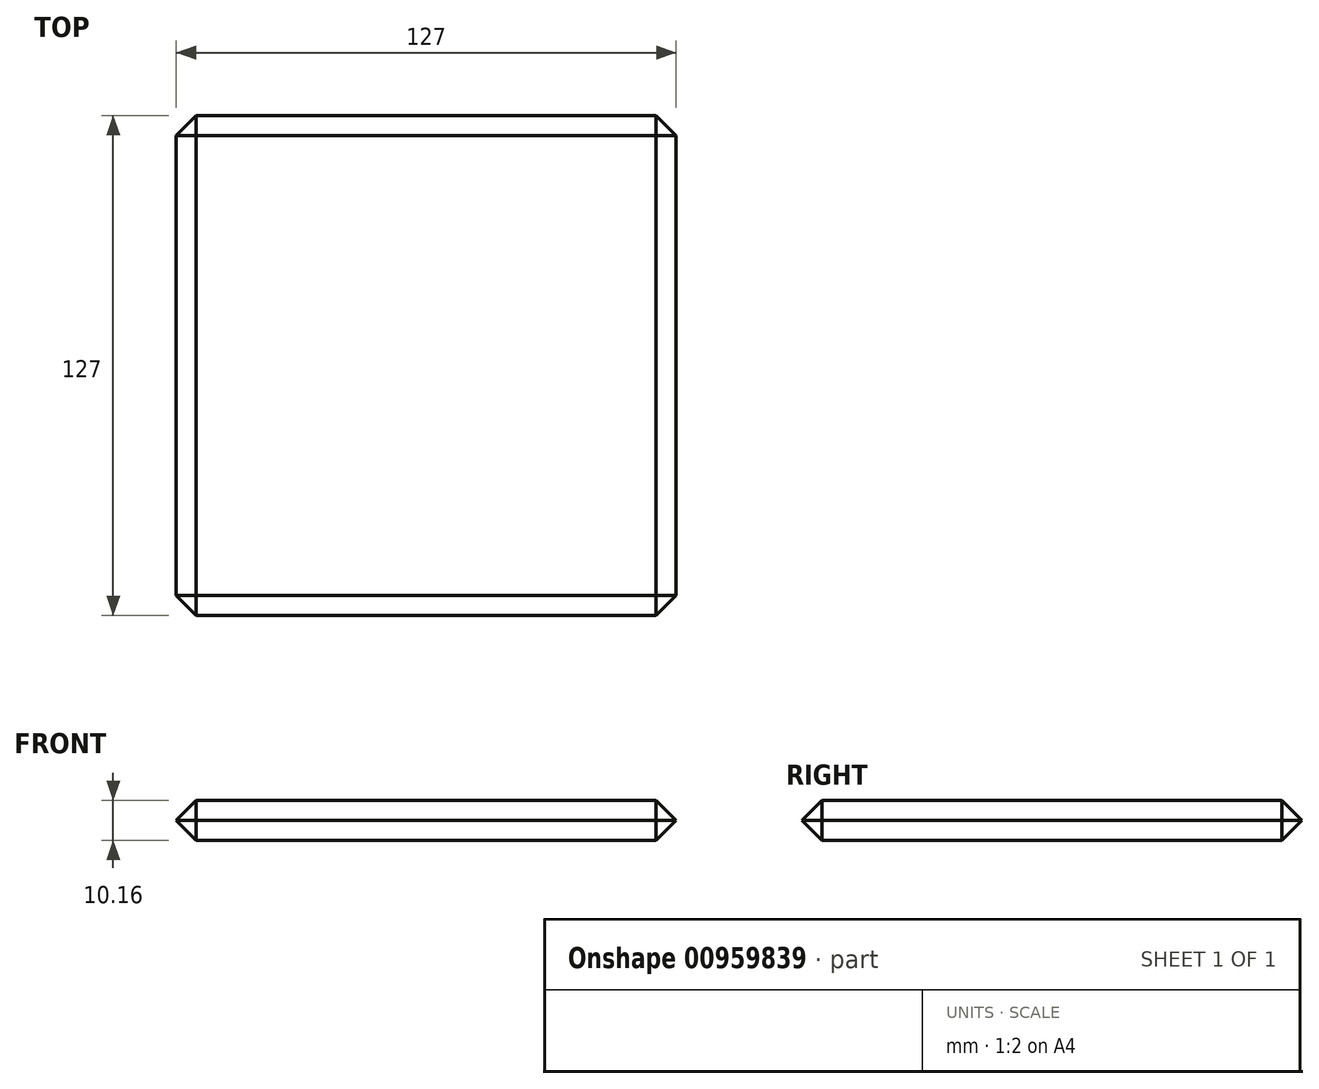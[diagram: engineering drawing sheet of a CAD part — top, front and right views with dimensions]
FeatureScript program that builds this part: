
annotation { "Feature Type Name" : "Feature", "Feature Type Description" : "" }
export const myFeature = defineFeature(function(context is Context, id is Id, definition is map)
    precondition{}
    {
        {
            var Q0;
            Q0=qCreatedBy(makeId("Top.planeOp"),FACE);
            var sketch = newSketch(context, id + "F0", { "sketchPlane" : qUnion([Q0])});
            skLineSegment(sketch, "E0.bottom", {"start": v(63.5, -63.5) * mm, "end": v(-63.5, -63.5) * mm});
            skLineSegment(sketch, "E0.top", {"start": v(63.5, 63.5) * mm, "end": v(-63.5, 63.5) * mm});
            skLineSegment(sketch, "E0.left", {"start": v(63.5, -63.5) * mm, "end": v(63.5, 63.5) * mm});
            skLineSegment(sketch, "E0.right", {"start": v(-63.5, -63.5) * mm, "end": v(-63.5, 63.5) * mm});
            skPoint(sketch, "E0.middle", {"position": v(0, 0) * mm});
            skSolve(sketch);
        }
        {
            var Q0;
            Q0 = qSketchRegion(id + "F0", true);
            extrude(context, id + "F1", {"entities" : qUnion([Q0]), "endBound" : BoundingType.SYMMETRIC, "depth" : 10.16 * mm, "offsetDistance" : 25.4 * mm});
        }
        {
            var Q0;
            Q0=makeQuery(id+"F1.opExtrude","SWEPT_FACE",FACE,{"disambiguationData":[OSD([sQuery(id+"F0.wireOp",EDGE,"E0.bottom")])]});
            var Q1;
            Q1=makeQuery(id+"F1.opExtrude","SWEPT_FACE",FACE,{"disambiguationData":[OSD([sQuery(id+"F0.wireOp",EDGE,"E0.top")])]});
            var Q2;
            Q2=makeQuery(id+"F1.opExtrude","SWEPT_FACE",FACE,{"disambiguationData":[OSD([sQuery(id+"F0.wireOp",EDGE,"E0.left")])]});
            var Q3;
            Q3=makeQuery(id+"F1.opExtrude","SWEPT_FACE",FACE,{"disambiguationData":[OSD([sQuery(id+"F0.wireOp",EDGE,"E0.right")])]});
            var Q4;
            Q4=makeQuery(id+"F1.opExtrude","CAP_EDGE",EDGE,{"disambiguationData":[OSD([sQuery(id+"F0.wireOp",EDGE,"E0.right")])],"isStart":false});
            var Q5;
            Q5=makeQuery(id+"F1.opExtrude","CAP_EDGE",EDGE,{"disambiguationData":[OSD([sQuery(id+"F0.wireOp",EDGE,"E0.top")])],"isStart":false});
            var Q6;
            Q6=makeQuery(id+"F1.opExtrude","CAP_EDGE",EDGE,{"disambiguationData":[OSD([sQuery(id+"F0.wireOp",EDGE,"E0.left")])],"isStart":false});
            var Q7;
            Q7=makeQuery(id+"F1.opExtrude","CAP_EDGE",EDGE,{"disambiguationData":[OSD([sQuery(id+"F0.wireOp",EDGE,"E0.bottom")])],"isStart":false});
            chamfer(context, id + "F2", {"entities" : qUnion([Q0, Q1, Q2, Q3, Q4, Q5, Q6, Q7]), "width" : 5.08 * mm, "tangentPropagation" : true});
        }
    });
